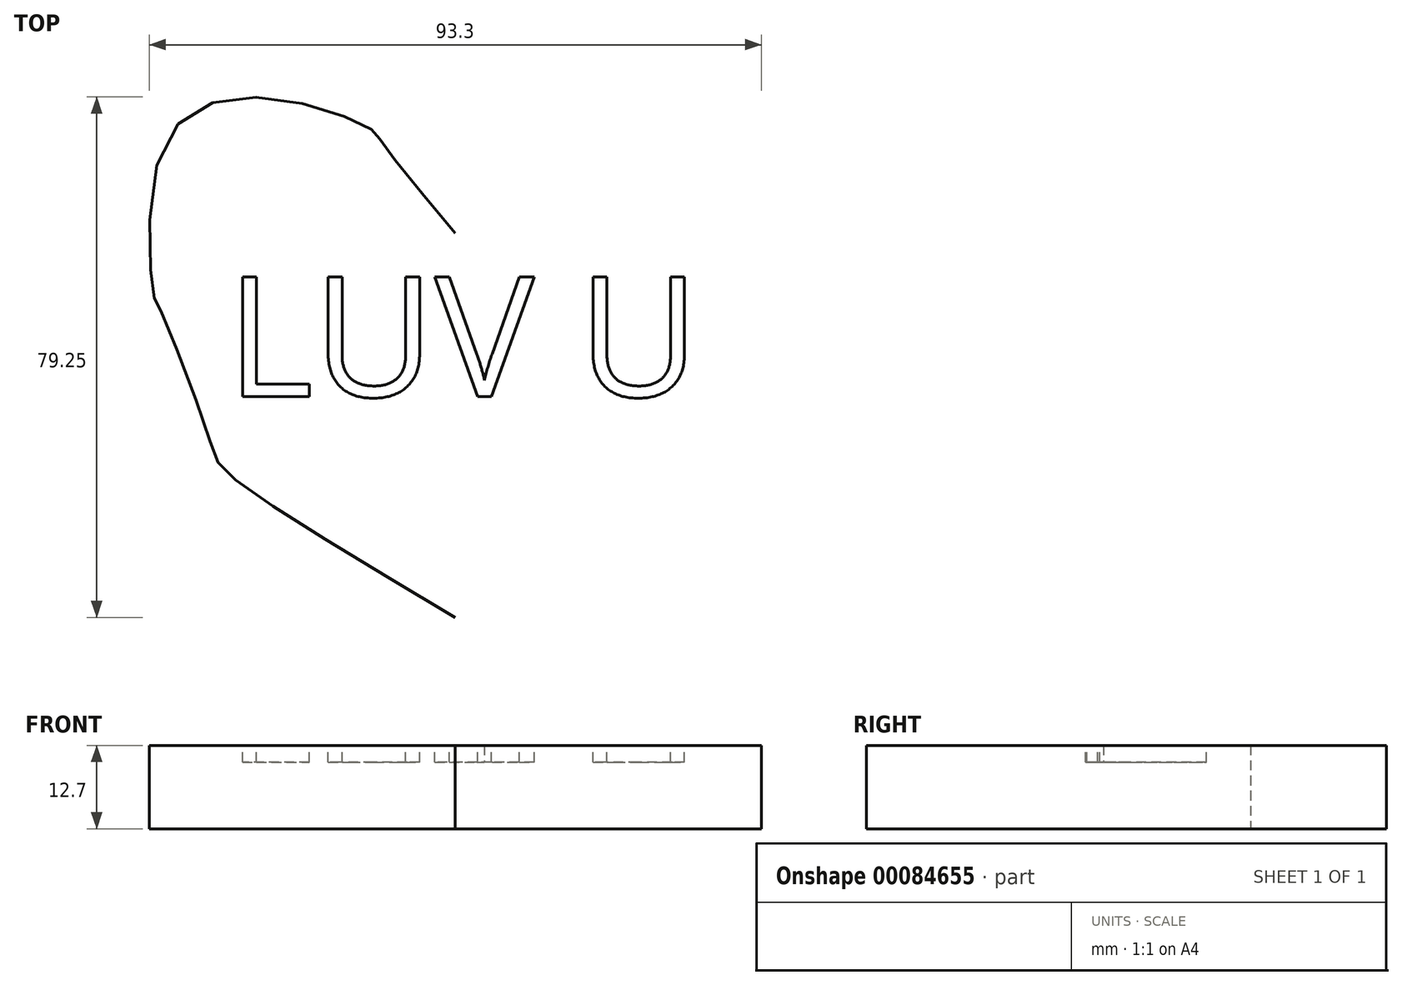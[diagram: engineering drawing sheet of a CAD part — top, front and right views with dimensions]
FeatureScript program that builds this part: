
annotation { "Feature Type Name" : "Feature", "Feature Type Description" : "" }
export const myFeature = defineFeature(function(context is Context, id is Id, definition is map)
    precondition{}
    {
        {
            var Q0;
            Q0=qCreatedBy(makeId("Top.planeOp"),FACE);
            var sketch = newSketch(context, id + "F0", { "sketchPlane" : qUnion([Q0])});
            skFitSpline(sketch, "E0", {"points": [v(0, 0) * mm, v(-11.48, 14.26) * mm, v(-12.46, 15.58) * mm, v(-27.55, 20.5) * mm, v(-44.27, 13.6) * mm, v(-45.9, -9.67) * mm, v(-45.25, -10.99) * mm, v(-37.38, -31.64) * mm, v(-35.09, -36.24) * mm, v(0, -58.53) * mm], "startDerivative": vector(-118.9, 141.96) * mm, "endDerivative": vector(239.46, -142.31) * mm});
            skLineSegment(sketch, "E1", {"start": v(0, 0) * mm, "end": v(0, -58.53) * mm});
            skSolve(sketch);
        }
        {
            var Q0;
            Q0 = qSketchRegion(id + "F0", true);
            extrude(context, id + "F1", {"entities" : qUnion([Q0]), "depth" : 12.7 * mm});
        }
        {
            var Q0;
            Q0=makeQuery(id+"F1.opExtrude","SWEPT_BODY",BODY,{"disambiguationData":[OSD([sQuery(id+"F0.wireOp",EDGE,"E0"),sQuery(id+"F0.wireOp",EDGE,"E1")])]});
            var Q1;
            Q1=qCreatedBy(makeId("Right.planeOp"),FACE);
            mirror(context, id + "F2", {"operationType" : NewBodyOperationType.ADD, "entities" : qUnion([Q0]), "mirrorPlane" : qUnion([Q1])});
        }
        {
            var Q0;
            {var subQ0=makeQuery(id+"F1.opExtrude","CAP_FACE",FACE,{"disambiguationData":[OSD([sQuery(id+"F0.wireOp",EDGE,"E0"),sQuery(id+"F0.wireOp",EDGE,"E1")])],"isStart":false});Q0=makeQuery(id+"F2.boolean.opBoolean","MERGE",FACE,{"derivedFrom":[subQ0,makeQuery(id+"F2.opPattern","COPY",FACE,{"derivedFrom":subQ0,"instanceName":"1"})]});}
            var sketch = newSketch(context, id + "F3", { "sketchPlane" : qUnion([Q0])});
            skText(sketch, "E2", { "text": "LUV U", "fontName": "OpenSans-Regular.ttf"});
            const initialGuessF3  = {"E2": [-0.03492, -0.0249, 1, 0, 0.01836]};
            skSetInitialGuess(sketch, initialGuessF3);
            skSolve(sketch);
        }
        {
            var Q0;
            Q0 = qSketchRegion(id + "F3", true);
            extrude(context, id + "F4", {"entities" : qUnion([Q0]), "operationType" : NewBodyOperationType.REMOVE, "oppositeDirection" : true, "depth" : 2.54 * mm});
        }
    });
